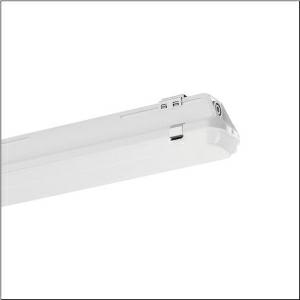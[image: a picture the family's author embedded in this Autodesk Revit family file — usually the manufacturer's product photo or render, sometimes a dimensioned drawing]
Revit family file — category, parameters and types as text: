
# Revit family: monsun_r__11_51fp20dp4b0u007_7a38
name_source: partatom
category: Lighting Fixtures
units: mm (PartAtom-declared; Revit-internal decimal feet)

## family parameters
Cut with Voids When Loaded = No
Host = Face
Light Source = No
Part Type = Normal
Room Calculation Point = No
Round Connector Dimension = Use Diameter
Shared = No

## types (1)
- --- (1 x LED, 10950 lm, 63.7 W, 4000K)
    Apparent Load = 64 VA
    CIE Flux Codes = 45 75 93 94 100
    Color Rendering = 80
    Color Temperature = 4000K
    Default Elevation = 1800 mm
    Description = Monsun® 11, damp-proof luminaire, chain hanger, primary optical cover: enclosure, of PC, light emission: direct distribution, primary light characteristic: symmetric, installation type: suspended mounting, surface-mounted, horizontal mounting, vertical mounting, LED, rated luminous flux: 10.950lm, luminous efficacy: 172lm/W, light colour: 840, colour temperature: 4000K, control gear: DALI 2, with terminal, 5-pole, max. 2.5mm², through-wiring: 7x 2.5mm², mains connection: 220..240V, AC, 50/60Hz, rated input power: 64W, housing, of glass-fibre reinforced polyester, uncoated, bright grey, incl. chain hanger, length: 1.590mm, width: 90mm, height: 88mm, clip for enclosure, of stainless steel (V2A), ceiling mounting element, of stainless steel (V2A), chain hanger, of stainless steel (V2A), protection rating (complete): IP66, insulation class (complete): insulation class I (protective earthing), certification: CE, ENEC, VDE, UKCA, protection symbol: D, impact resistance: IK08, permissible operating ambient temperature: -40..+35°C, standard: EN 50419, EN 60598-2-1, contact your sales advisor before using the luminaires in applications with unclear chemical exposure, large temperature fluctuations or condensation-forming humidity, LABS conformity tested according to VDMA 24364:2018-05, no direct snow, no direct sun, no direct rain, for indoor or canopied outdoor use, corresponds to IFS (International Featured Standards) requirements for safety and quality in the food industry, packaging unit: 1 piece
    Height = 89 mm
    Lamp = 1 x LED
    Lamp Light Flux = 10950 lm
    Lamp Power = 63.7 W
    Lamp count = 1
    Length = 1590 mm
    Luminous efficacy = 172 lm/W
    Manufacturer = Siteco
    ModVariant = No
    Model = 51FP20DP4B0U007
    Mounting Place = Ceiling
    Mounting Type = Surface mounted
    Number of Poles = 1
    OnlyDefault = Yes
    Power Factor = 1
    Product Name = Monsun® 11
    Product group = damp-proof luminaire
    ProductGroupID = 300
    Protection Class = Protection class I
    Protection Degree = IP 66
    RLX_Detail_Level = 1
    RLX_Emergency_Light_Flux = 0 lm
    RLX_Emergency_Type = 0
    RLX_Emergency_Type_DB = No
    RlxData = <blob elided: 92229 chars, md5=06c92ee7>
    Socket = socket
    Standby Power = 0 W
    System Light Flux = 10950 lm
    System Power = 64 W
    Type Comments = factory setting: luminous flux: 100 % | dim-lin: 254 | 441 mA
    Type Image = l_1349237.jpg
    URL = http://relux.com
    VarID = @adj_022948
    Voltage = 0 V
    Weight = 0.00 kg
    Width = 90 mm

## geometry (parser evidence)
native form markers: Blend x4, Sweep x13
no freeform markers — native parametric forms only
